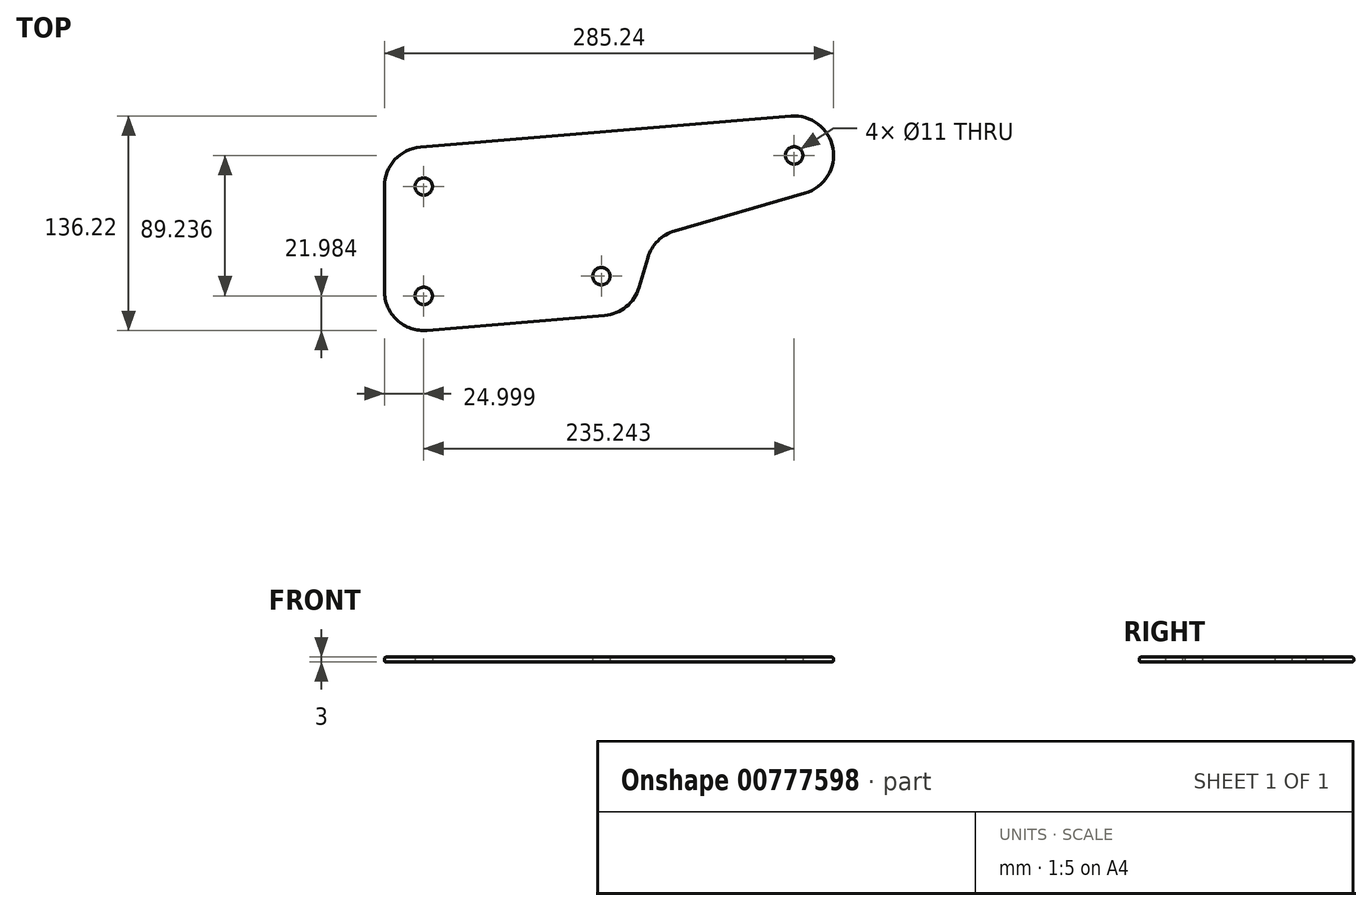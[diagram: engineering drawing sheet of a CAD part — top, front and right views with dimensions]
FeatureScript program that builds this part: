
annotation { "Feature Type Name" : "Feature", "Feature Type Description" : "" }
export const myFeature = defineFeature(function(context is Context, id is Id, definition is map)
    precondition{}
    {
        {
            var Q0;
            Q0=qCreatedBy(makeId("Top.planeOp"),FACE);
            var sketch = newSketch(context, id + "F0", { "sketchPlane" : qUnion([Q0])});
            skLineSegment(sketch, "E0", {"start": v(-140.51, 0) * mm, "end": v(157, 0) * mm, "construction": true});
            skCircle(sketch, "E1", {"center": v(0, 0) * mm, "radius": 5.5 * mm});
            skCircle(sketch, "E2", {"center": v(-112.81, -12.49) * mm, "radius": 5.5 * mm});
            skCircle(sketch, "E3", {"center": v(-112.81, 57.01) * mm, "radius": 5.5 * mm});
            skCircle(sketch, "E4", {"center": v(122.43, 76.75) * mm, "radius": 5.5 * mm});
            skLineSegment(sketch, "E5", {"start": v(-137.81, 57.01) * mm, "end": v(-137.81, -9.47) * mm});
            skArc(sketch, "E6", {"start": v(-114.9, 81.93) * mm, "mid": v(-131.21, 73.94) * mm, "end": v(-137.81, 57.01) * mm});
            skLineSegment(sketch, "E7", {"start": v(46.58, 28.74) * mm, "end": v(129.4, 52.74) * mm});
            skLineSegment(sketch, "E8.trimOffspring", {"start": v(120.34, 101.66) * mm, "end": v(-114.9, 81.93) * mm});
            skArc(sketch, "E9", {"start": v(129.4, 52.74) * mm, "mid": v(147.02, 81.3) * mm, "end": v(120.34, 101.66) * mm});
            skArc(sketch, "E10.filletArc", {"start": v(-137.81, -9.47) * mm, "mid": v(-129.73, -27.88) * mm, "end": v(-110.72, -34.39) * mm});
            skLineSegment(sketch, "E11", {"start": v(23.97, -7.1) * mm, "end": v(29.57, 11.82) * mm});
            skLineSegment(sketch, "E12", {"start": v(2.1, -24.91) * mm, "end": v(-110.72, -34.39) * mm});
            skPoint(sketch, "E13.visualSharp", {"position": v(19.12, -23.48) * mm});
            skArc(sketch, "E13.filletArc", {"start": v(2.1, -24.91) * mm, "mid": v(15.79, -19.39) * mm, "end": v(23.97, -7.1) * mm});
            skPoint(sketch, "E14.visualSharp", {"position": v(33.45, 24.93) * mm});
            skArc(sketch, "E14.filletArc", {"start": v(46.58, 28.74) * mm, "mid": v(35.92, 22.45) * mm, "end": v(29.57, 11.82) * mm});
            skSolve(sketch);
        }
        {
            var Q0;
            Q0=makeQuery(id+"F0.imprint","IMPRINT",FACE,{"disambiguationData":[TD([[makeQuery(id+"F0.imprint","IMPRINT",EDGE,{"derivedFrom":sQuery(id+"F0.wireOp",EDGE,"E1")}),-1.0]])]});
            extrude(context, id + "F1", {"entities" : qUnion([Q0]), "depth" : 3 * mm, "offsetDistance" : 25 * mm});
        }
        {
            var Q0;
            Q0=makeQuery(id+"F1.opExtrude","CAP_EDGE",EDGE,{"disambiguationData":[OSD([sQuery(id+"F0.wireOp",EDGE,"E8.trimOffspring")])],"isStart":true});
            var Q1;
            Q1=makeQuery(id+"F1.opExtrude","CAP_EDGE",EDGE,{"disambiguationData":[OSD([sQuery(id+"F0.wireOp",EDGE,"E9")])],"isStart":true});
            var Q2;
            Q2=makeQuery(id+"F1.opExtrude","CAP_EDGE",EDGE,{"disambiguationData":[OSD([sQuery(id+"F0.wireOp",EDGE,"E7")])],"isStart":true});
            var Q3;
            Q3=makeQuery(id+"F1.opExtrude","CAP_EDGE",EDGE,{"disambiguationData":[OSD([sQuery(id+"F0.wireOp",EDGE,"ydMExbMu-Qene-057d-PmfW-8A1b4pkeo0xo")])],"isStart":true});
            var Q4;
            Q4=makeQuery(id+"F1.opExtrude","CAP_EDGE",EDGE,{"disambiguationData":[OSD([sQuery(id+"F0.wireOp",EDGE,"wCUxGTr0-vM4G-2Crd-imUJ-0EBYBc7c8Rgm")])],"isStart":true});
            var Q5;
            Q5=makeQuery(id+"F1.opExtrude","CAP_EDGE",EDGE,{"disambiguationData":[OSD([sQuery(id+"F0.wireOp",EDGE,"2yJgQXgX-vCvG-lJXJ-8XKU-Pv17DjZZOOpr")])],"isStart":true});
            var Q6;
            Q6=makeQuery(id+"F1.opExtrude","CAP_EDGE",EDGE,{"disambiguationData":[OSD([sQuery(id+"F0.wireOp",EDGE,"E5")])],"isStart":true});
            var Q7;
            Q7=makeQuery(id+"F1.opExtrude","CAP_EDGE",EDGE,{"disambiguationData":[OSD([sQuery(id+"F0.wireOp",EDGE,"E5")])],"isStart":false});
            var Q8;
            Q8=makeQuery(id+"F1.opExtrude","CAP_EDGE",EDGE,{"disambiguationData":[OSD([sQuery(id+"F0.wireOp",EDGE,"2yJgQXgX-vCvG-lJXJ-8XKU-Pv17DjZZOOpr")])],"isStart":false});
            var Q9;
            Q9=makeQuery(id+"F1.opExtrude","CAP_EDGE",EDGE,{"disambiguationData":[OSD([sQuery(id+"F0.wireOp",EDGE,"E6")])],"isStart":true});
            var Q10;
            Q10=makeQuery(id+"F1.opExtrude","CAP_EDGE",EDGE,{"disambiguationData":[OSD([sQuery(id+"F0.wireOp",EDGE,"E6")])],"isStart":false});
            var Q11;
            Q11=makeQuery(id+"F1.opExtrude","CAP_EDGE",EDGE,{"disambiguationData":[OSD([sQuery(id+"F0.wireOp",EDGE,"E8.trimOffspring")])],"isStart":false});
            var Q12;
            Q12=makeQuery(id+"F1.opExtrude","CAP_EDGE",EDGE,{"disambiguationData":[OSD([sQuery(id+"F0.wireOp",EDGE,"E9")])],"isStart":false});
            var Q13;
            Q13=makeQuery(id+"F1.opExtrude","CAP_EDGE",EDGE,{"disambiguationData":[OSD([sQuery(id+"F0.wireOp",EDGE,"E7")])],"isStart":false});
            var Q14;
            Q14=makeQuery(id+"F1.opExtrude","CAP_EDGE",EDGE,{"disambiguationData":[OSD([sQuery(id+"F0.wireOp",EDGE,"ydMExbMu-Qene-057d-PmfW-8A1b4pkeo0xo")])],"isStart":false});
            var Q15;
            Q15=makeQuery(id+"F1.opExtrude","CAP_EDGE",EDGE,{"disambiguationData":[OSD([sQuery(id+"F0.wireOp",EDGE,"wCUxGTr0-vM4G-2Crd-imUJ-0EBYBc7c8Rgm")])],"isStart":false});
            fillet(context, id + "F2", {"entities" : qUnion([Q0, Q1, Q2, Q3, Q4, Q5, Q6, Q7, Q8, Q9, Q10, Q11, Q12, Q13, Q14, Q15]), "radius" : 1 * mm, "tangentPropagation" : true, "allowEdgeOverflow" : false});
        }
    });
